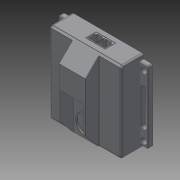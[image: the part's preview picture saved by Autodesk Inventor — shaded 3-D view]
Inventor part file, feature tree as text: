
AUTODESK INVENTOR PART (.ipt)
format: ipt  version: 2015 SP1 (Build 190203100, 203)  size: 401,408 bytes
history: native  units: mm
features: extrude x10, sketch x10, fillet x9, chamfer x2
ambient origin geometry x8: Origin, YZ Plane, XZ Plane, XY Plane, X Axis, Y Axis, Z Axis, Center Point
bodies: Solid1 (feature_tree)
feature tree (31):
  extrude  "Extrusion1"  Depth=80.0mm
  extrude  "Extrusion2"  Depth=10.0mm
  extrude  "Extrusion3"  Depth=10.0mm
  extrude  "Extrusion4"  Depth=5.0mm TaperAngle=0.0deg
  chamfer  "Chamfer1"  Distance=20.0mm
  extrude  "Extrusion5"  Depth=17.0mm TaperAngle=45.0deg
  chamfer  "Chamfer2"  Distance=2.0mm
  fillet  "Fillet1"  Radius=2.0mm
  fillet  "Fillet2"  Radius=15.0mm
  fillet  "Fillet3"  Radius=15.0mm
  fillet  "Fillet4"  Radius=0.5mm
  extrude  "Extrusion6"  Depth=0.5mm
  extrude  "Extrusion7"  Depth=0.5mm
  fillet  "Fillet5"  Radius=2.0mm
  extrude  "Extrusion8"  Depth=12.0mm TaperAngle=0.0deg
  fillet  "Fillet6"  Radius=12.0mm
  fillet  "Fillet7"  Radius=2.0mm
  fillet  "Fillet8"  Radius=22.0mm
  fillet  "Fillet9"  Radius=2.0mm
  extrude  "Extrusion9"  Depth=12.0mm
  extrude  "Extrusion10"  Depth=12.0mm
  sketch  "Sketch1"  dims[d0=80.0mm d1=90.0mm]
  sketch  "Sketch2"  dims[d2=25.0mm d3=0.0mm d4=10.0mm]
  sketch  "Sketch3"  dims[d5=5.0mm d6=10.0mm]
  sketch  "Sketch4"  dims[d7=5.0mm d8=5.0mm d9=0.0mm]
  sketch  "Sketch5"  dims[d10=6.0mm]
  sketch  "Sketch6"  dims[d11=6.0mm]
  sketch  "Sketch7"  dims[d12=6.0mm]
  sketch  "Sketch8"  dims[d13=6.0mm d14=20.0mm d15=0.0mm]
  sketch  "Sketch9"  dims[d18=15.0mm d19=0.0mm d20=17.0mm d21=2.0mm d22=45.0deg]
  sketch  "Sketch10"  dims[d23=25.0mm d24=2.0mm d25=2.0mm d26=15.0mm d27=0.0mm d28=15.0mm d29=2.0mm d30=8.726646mm d31=0.5mm d32=0.5mm d33=0.5mm d34=2.0mm d37=12.0mm d38=0.0mm d39=12.0mm d40=0.0mm d41=2.0mm d42=22.0mm d43=2.0mm d44=0.0mm d45=0.2mm d46=1.5mm d47=0.7mm d48=0.5mm d49=22.0mm d50=12.0mm d51=12.0mm d52=0.0mm d55=12.0mm d56=0.0mm]
